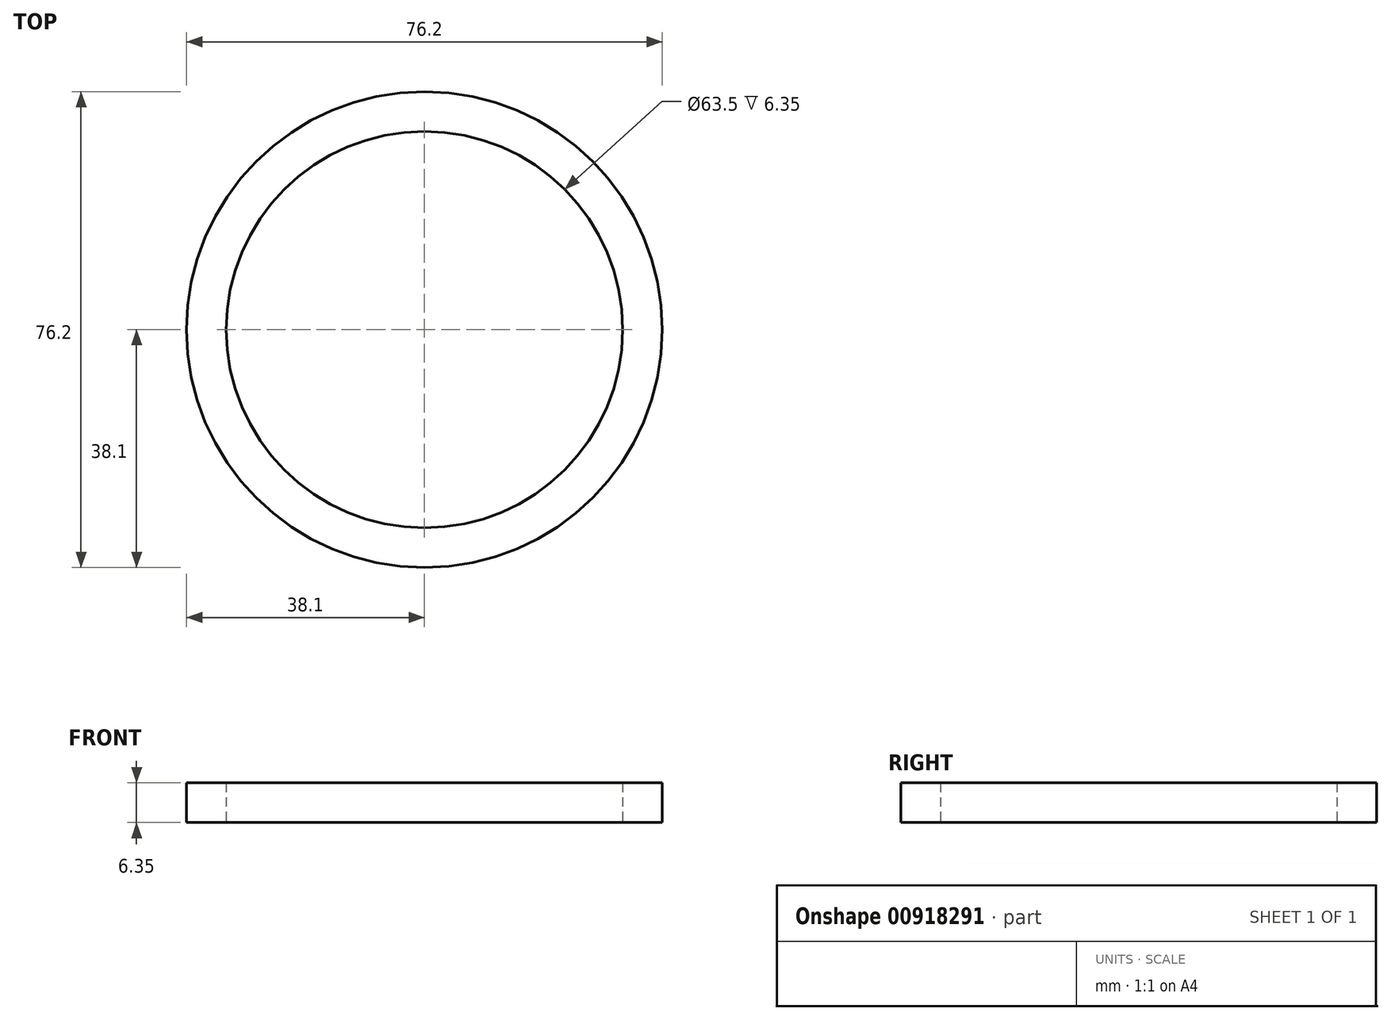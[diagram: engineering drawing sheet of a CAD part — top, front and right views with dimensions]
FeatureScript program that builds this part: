
annotation { "Feature Type Name" : "Feature", "Feature Type Description" : "" }
export const myFeature = defineFeature(function(context is Context, id is Id, definition is map)
    precondition{}
    {
        {
            var Q0;
            Q0=qCreatedBy(makeId("Top.planeOp"),FACE);
            var sketch = newSketch(context, id + "F0", { "sketchPlane" : qUnion([Q0])});
            skCircle(sketch, "E0", {"center": v(0, 0) * mm, "radius": 38.1 * mm});
            skCircle(sketch, "E1", {"center": v(0, 0) * mm, "radius": 31.75 * mm});
            skSolve(sketch);
        }
        {
            var Q0;
            Q0=makeQuery(id+"F0.imprint","IMPRINT",FACE,{"disambiguationData":[TD([[makeQuery(id+"F0.imprint","IMPRINT",EDGE,{"derivedFrom":sQuery(id+"F0.wireOp",EDGE,"E0")}),1.0]])]});
            extrude(context, id + "F1", {"entities" : qUnion([Q0]), "depth" : 6.35 * mm, "offsetDistance" : 25.4 * mm});
        }
    });
